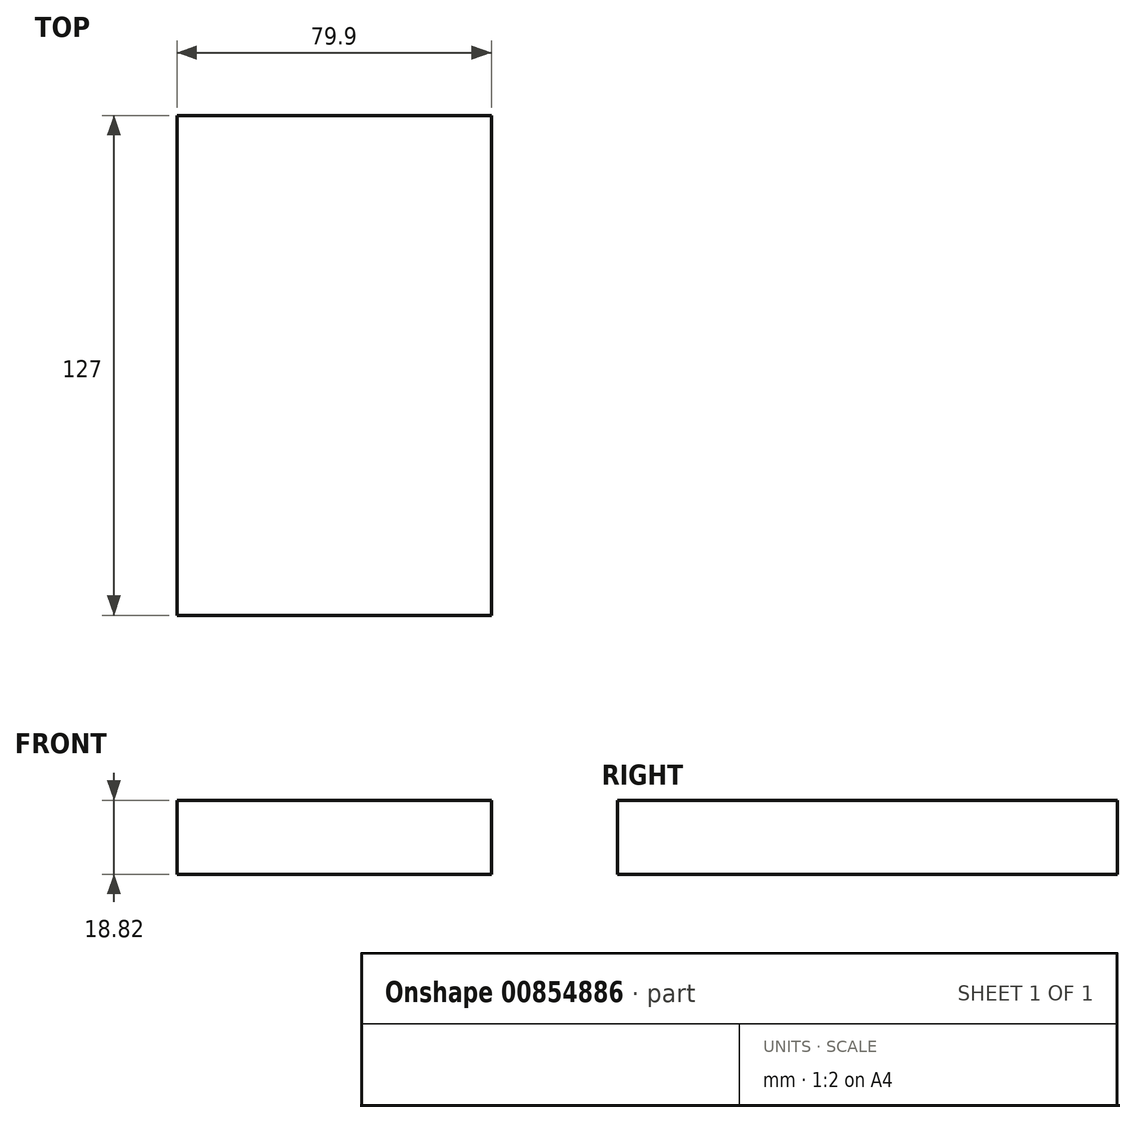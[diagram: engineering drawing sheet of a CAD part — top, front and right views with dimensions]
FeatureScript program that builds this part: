
annotation { "Feature Type Name" : "Feature", "Feature Type Description" : "" }
export const myFeature = defineFeature(function(context is Context, id is Id, definition is map)
    precondition{}
    {
        {
            var Q0;
            Q0=qCreatedBy(makeId("Front.planeOp"),FACE);
            var sketch = newSketch(context, id + "F0", { "sketchPlane" : qUnion([Q0])});
            skLineSegment(sketch, "E0.bottom", {"start": v(-39.95, 9.41) * mm, "end": v(39.95, 9.41) * mm});
            skLineSegment(sketch, "E0.top", {"start": v(-39.95, -9.41) * mm, "end": v(39.95, -9.41) * mm});
            skLineSegment(sketch, "E0.left", {"start": v(-39.95, 9.41) * mm, "end": v(-39.95, -9.41) * mm});
            skLineSegment(sketch, "E0.right", {"start": v(39.95, 9.41) * mm, "end": v(39.95, -9.41) * mm});
            skPoint(sketch, "E0.middle", {"position": v(0, 0) * mm});
            skLineSegment(sketch, "E1.bottom", {"start": v(113.66, 39.45) * mm, "end": v(66.8, 39.45) * mm});
            skLineSegment(sketch, "E1.top", {"start": v(113.66, 70.7) * mm, "end": v(66.8, 70.7) * mm});
            skLineSegment(sketch, "E1.left", {"start": v(113.66, 39.45) * mm, "end": v(113.66, 70.7) * mm});
            skLineSegment(sketch, "E1.right", {"start": v(66.8, 39.45) * mm, "end": v(66.8, 70.7) * mm});
            skPoint(sketch, "E1.middle", {"position": v(90.23, 55.08) * mm});
            skLineSegment(sketch, "E2", {"start": v(39.95, 9.41) * mm, "end": v(39.95, 36.85) * mm});
            skArc(sketch, "E3", {"start": v(39.95, 36.85) * mm, "mid": v(42.78, 43.67) * mm, "end": v(49.6, 46.5) * mm});
            skLineSegment(sketch, "E4", {"start": v(49.6, 46.5) * mm, "end": v(74.4, 46.5) * mm});
            skLineSegment(sketch, "E5.0", {"start": v(49.6, 65.55) * mm, "end": v(74.4, 65.55) * mm});
            skArc(sketch, "E5.1", {"start": v(20.9, 36.85) * mm, "mid": v(29.31, 57.14) * mm, "end": v(49.6, 65.55) * mm});
            skLineSegment(sketch, "E5.2", {"start": v(20.9, 9.41) * mm, "end": v(20.9, 36.85) * mm});
            skFitSpline(sketch, "E6", {"points": [v(49.6, 65.55) * mm, v(-39.95, 9.41) * mm], "startDerivative": vector(-116.66, -0.18) * mm, "endDerivative": vector(-0.6, -121.37) * mm});
            skSolve(sketch);
        }
        {
            var Q0;
            Q0=makeQuery(id+"F0.imprint","IMPRINT",FACE,{"disambiguationData":[TD([[makeQuery(id+"F0.imprint","IMPRINT",EDGE,{"derivedFrom":sQuery(id+"F0.wireOp",EDGE,"E0.top")}),1.0]])]});
            extrude(context, id + "F1", {"entities" : qUnion([Q0]), "endBound" : BoundingType.SYMMETRIC, "depth" : 127 * mm, "offsetDistance" : 25.4 * mm});
        }
    });
